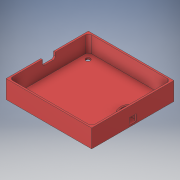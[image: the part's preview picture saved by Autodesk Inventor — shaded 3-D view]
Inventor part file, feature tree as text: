
AUTODESK INVENTOR PART (.ipt)
format: ipt  version: 2019 (Build 230136000, 136)  size: 186,880 bytes
history: native  units: mm
features: extrude x5, sketch x5, fillet x2, other x1, shell x1
ambient origin geometry x8: Origin, YZ Plane, XZ Plane, XY Plane, X Axis, Y Axis, Z Axis, Center Point
bodies: Body1 (feature_tree)
feature tree (14):
  other  "Твердое тело1"
  extrude  "Выдавливание1"  Depth=52.0mm
  shell  "Оболочка1"  Thickness=50.0mm
  extrude  "Выдавливание2"  Depth=11.0mm TaperAngle=0.0deg
  fillet  "Сопряжение1"  Radius=1.0mm
  fillet  "Сопряжение2"  Radius=7.4mm
  extrude  "Выдавливание4"  Depth=7.8mm
  extrude  "Выдавливание5"  Depth=11.0mm TaperAngle=0.0deg
  extrude  "Выдавливание7"  Depth=1.5mm
  sketch  "Эскиз1"
  sketch  "Эскиз2"
  sketch  "Эскиз4"
  sketch  "Эскиз5"
  sketch  "Эскиз8"
